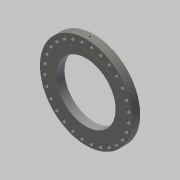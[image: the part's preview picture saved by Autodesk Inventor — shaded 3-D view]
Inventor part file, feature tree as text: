
AUTODESK INVENTOR PART (.ipt)
format: ipt  version: 2017.3 (Build 213257000, 257)  size: 276,480 bytes
history: native  units: in
note: dims shown in document units (in); Inventor stores cm internally (conversion verified against a paired STEP export)
features: other x3, extrude x1, sketch x1
ambient origin geometry x8: Origin, YZ Plane, XZ Plane, XY Plane, X Axis, Y Axis, Z Axis, Center Point
bodies: Solid1 (feature_tree)
feature tree (5):
  other  "A1-19010-100-01 30in CL300 RFBL flange.ipt"
  extrude  "Extrusion1"  Depth=0.0312in
  other  "Solid1::A1-19010-100-01 30in CL300 RFBL flange.ipt"
  other  "TaggingFeature1"
  sketch  "Sketch1"  dims[d0=0.3937in d1=3.6777in d2=0.0in d3=33.75in d4=0.0625in d5=0.0in d6=30.0in d7=2.0in d8=0.0in d11=0.0in d12=39.25in d13=0.0442in d14=1.875in d21=11.0236in d22=360.0deg d24=0.0625in d28=0.0312in d31=0.0312in d32=0.0in d33=0.0625in d36=1.8701in d38=2.0in d42=2.5in d43=0.8108in d44=0.7874in d45=360.0deg d9=30.0in d10=27.5in d15=3.7402in d16=0.0in]
